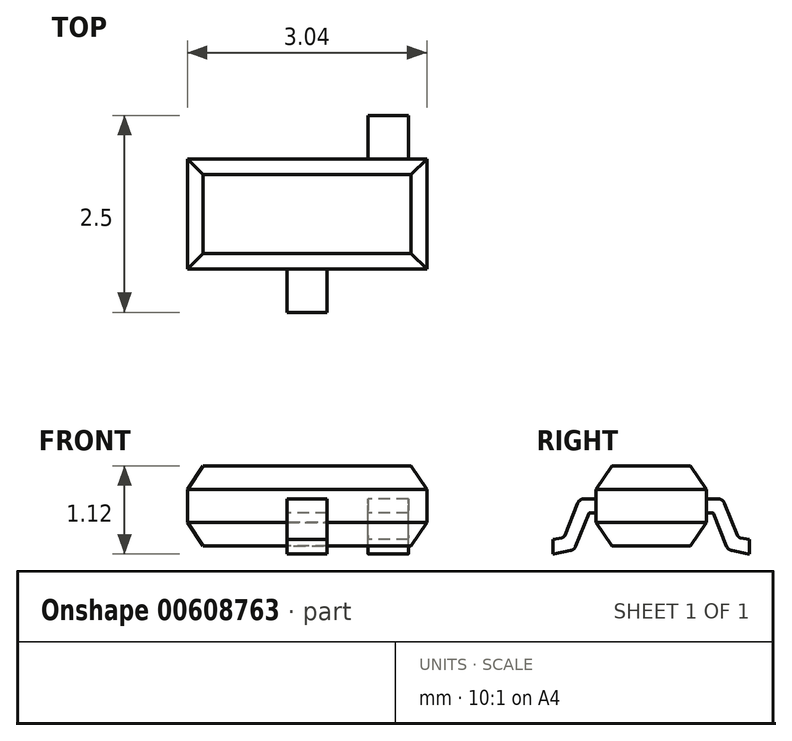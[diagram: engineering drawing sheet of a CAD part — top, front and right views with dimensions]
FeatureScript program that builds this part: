
annotation { "Feature Type Name" : "Feature", "Feature Type Description" : "" }
export const myFeature = defineFeature(function(context is Context, id is Id, definition is map)
    precondition{}
    {
        {
            var Q0;
            Q0=qCreatedBy(makeId("Top.planeOp"),FACE);
            cPlane(context, id + "F0", {"entities" : qUnion([Q0]), "cplaneType" : CPlaneType.OFFSET, "offset" : 0.1 * mm, "width" : 150 * mm, "height" : 150 * mm});
        }
        {
            var Q0;
            Q0=qCreatedBy(id+"F0.planeOp",FACE);
            var sketch = newSketch(context, id + "F1", { "sketchPlane" : qUnion([Q0])});
            skLineSegment(sketch, "E0.bottom", {"start": v(-1.52, 0.7) * mm, "end": v(1.52, 0.7) * mm});
            skLineSegment(sketch, "E0.top", {"start": v(-1.52, -0.7) * mm, "end": v(1.52, -0.7) * mm});
            skLineSegment(sketch, "E0.left", {"start": v(-1.52, 0.7) * mm, "end": v(-1.52, -0.7) * mm});
            skLineSegment(sketch, "E0.right", {"start": v(1.52, 0.7) * mm, "end": v(1.52, -0.7) * mm});
            skPoint(sketch, "E0.middle", {"position": v(0, 0) * mm});
            skSolve(sketch);
        }
        {
            var Q0;
            Q0=makeQuery(id+"F1.imprint","IMPRINT",FACE,{"disambiguationData":[TD([[makeQuery(id+"F1.imprint","IMPRINT",EDGE,{"derivedFrom":sQuery(id+"F1.wireOp",EDGE,"E0.bottom")}),-1.0]])]});
            extrude(context, id + "F2", {"entities" : qUnion([Q0]), "depth" : 1.02 * mm, "offsetDistance" : 25 * mm});
        }
        {
            var Q0;
            Q0=makeQuery(id+"F2.opExtrude","CAP_EDGE",EDGE,{"disambiguationData":[OSD([sQuery(id+"F1.wireOp",EDGE,"E0.left")])],"isStart":false});
            var Q1;
            Q1=makeQuery(id+"F2.opExtrude","CAP_EDGE",EDGE,{"disambiguationData":[OSD([sQuery(id+"F1.wireOp",EDGE,"E0.left")])],"isStart":true});
            var Q2;
            Q2=makeQuery(id+"F2.opExtrude","CAP_EDGE",EDGE,{"disambiguationData":[OSD([sQuery(id+"F1.wireOp",EDGE,"E0.right")])],"isStart":true});
            var Q3;
            Q3=makeQuery(id+"F2.opExtrude","CAP_EDGE",EDGE,{"disambiguationData":[OSD([sQuery(id+"F1.wireOp",EDGE,"E0.right")])],"isStart":false});
            chamfer(context, id + "F3", {"entities" : qUnion([Q0, Q1, Q2, Q3]), "chamferType" : ChamferType.TWO_OFFSETS, "width1" : 0.2 * mm, "oppositeDirection" : false, "width2" : 0.3 * mm, "tangentPropagation" : true});
        }
        {
            var Q0;
            Q0=makeQuery(id+"F2.opExtrude","CAP_EDGE",EDGE,{"disambiguationData":[OSD([sQuery(id+"F1.wireOp",EDGE,"E0.top")])],"isStart":false});
            var Q1;
            Q1=makeQuery(id+"F2.opExtrude","CAP_EDGE",EDGE,{"disambiguationData":[OSD([sQuery(id+"F1.wireOp",EDGE,"E0.top")])],"isStart":true});
            var Q2;
            Q2=makeQuery(id+"F2.opExtrude","CAP_EDGE",EDGE,{"disambiguationData":[OSD([sQuery(id+"F1.wireOp",EDGE,"E0.bottom")])],"isStart":true});
            var Q3;
            Q3=makeQuery(id+"F2.opExtrude","CAP_EDGE",EDGE,{"disambiguationData":[OSD([sQuery(id+"F1.wireOp",EDGE,"E0.bottom")])],"isStart":false});
            chamfer(context, id + "F4", {"entities" : qUnion([Q0, Q1, Q2, Q3]), "chamferType" : ChamferType.TWO_OFFSETS, "width1" : 0.2 * mm, "oppositeDirection" : false, "width2" : 0.3 * mm, "tangentPropagation" : true});
        }
        {
            var Q0;
            {var subQ0=sQuery(id+"F1.wireOp",EDGE,"E0.top");Q0=makeQuery(id+"F4.opChamfer","BLEND_EDGE",EDGE,{"blendedFrom":[makeQuery(id+"F2.opExtrude","CAP_EDGE",EDGE,{"disambiguationData":[OSD([subQ0])],"isStart":false}),makeQuery(id+"F2.opExtrude","CAP_FACE",FACE,{"disambiguationData":[OSD([sQuery(id+"F1.wireOp",EDGE,"E0.bottom"),subQ0,sQuery(id+"F1.wireOp",EDGE,"E0.left"),sQuery(id+"F1.wireOp",EDGE,"E0.right")])],"isStart":false})],"blendedInto":[makeQuery(id+"F2.opExtrude","CAP_FACE",FACE,{"disambiguationData":[OSD([sQuery(id+"F1.wireOp",EDGE,"E0.bottom"),subQ0,sQuery(id+"F1.wireOp",EDGE,"E0.left"),sQuery(id+"F1.wireOp",EDGE,"E0.right")])],"isStart":false})]});}
            cPoint(context, id + "F5", {"entities" : qUnion([Q0]), "parameter" : 0.5});
        }
        {
            var Q0;
            {var subQ0=sQuery(id+"F1.wireOp",EDGE,"E0.bottom");Q0=makeQuery(id+"F4.opChamfer","BLEND_EDGE",EDGE,{"blendedFrom":[makeQuery(id+"F2.opExtrude","CAP_EDGE",EDGE,{"disambiguationData":[OSD([subQ0])],"isStart":false}),makeQuery(id+"F2.opExtrude","CAP_FACE",FACE,{"disambiguationData":[OSD([subQ0,sQuery(id+"F1.wireOp",EDGE,"E0.top"),sQuery(id+"F1.wireOp",EDGE,"E0.left"),sQuery(id+"F1.wireOp",EDGE,"E0.right")])],"isStart":false})],"blendedInto":[makeQuery(id+"F2.opExtrude","CAP_FACE",FACE,{"disambiguationData":[OSD([subQ0,sQuery(id+"F1.wireOp",EDGE,"E0.top"),sQuery(id+"F1.wireOp",EDGE,"E0.left"),sQuery(id+"F1.wireOp",EDGE,"E0.right")])],"isStart":false})]});}
            cPoint(context, id + "F6", {"entities" : qUnion([Q0]), "parameter" : 0.5});
        }
        {
            var Q0;
            {var subQ0=sQuery(id+"F1.wireOp",EDGE,"E0.bottom");Q0=makeQuery(id+"F4.opChamfer","BLEND_EDGE",EDGE,{"blendedFrom":[makeQuery(id+"F2.opExtrude","CAP_EDGE",EDGE,{"disambiguationData":[OSD([subQ0])],"isStart":true}),makeQuery(id+"F2.opExtrude","CAP_FACE",FACE,{"disambiguationData":[OSD([subQ0,sQuery(id+"F1.wireOp",EDGE,"E0.top"),sQuery(id+"F1.wireOp",EDGE,"E0.left"),sQuery(id+"F1.wireOp",EDGE,"E0.right")])],"isStart":true})],"blendedInto":[makeQuery(id+"F2.opExtrude","CAP_FACE",FACE,{"disambiguationData":[OSD([subQ0,sQuery(id+"F1.wireOp",EDGE,"E0.top"),sQuery(id+"F1.wireOp",EDGE,"E0.left"),sQuery(id+"F1.wireOp",EDGE,"E0.right")])],"isStart":true})]});}
            cPoint(context, id + "F7", {"entities" : qUnion([Q0]), "parameter" : 0.5});
        }
        {
            var Q0;
            Q0 = qCreatedBy(id + "F5" ,VERTEX);
            var Q1;
            Q1 = qCreatedBy(id + "F6" ,VERTEX);
            var Q2;
            Q2 = qCreatedBy(id + "F7" ,VERTEX);
            cPlane(context, id + "F8", {"entities" : qUnion([Q0, Q1, Q2]), "cplaneType" : CPlaneType.THREE_POINT, "offset" : 25 * mm, "width" : 150 * mm, "height" : 150 * mm});
        }
        {
            var Q0;
            Q0=qCreatedBy(id+"F8.planeOp",FACE);
            var sketch = newSketch(context, id + "F9", { "sketchPlane" : qUnion([Q0])});
            skLineSegment(sketch, "E1", {"start": v(0, 0) * mm, "end": v(-2.5, 0) * mm, "construction": true});
            skLineSegment(sketch, "E2", {"start": v(-1.25, 0) * mm, "end": v(-1.25, 0.09) * mm});
            skLineSegment(sketch, "E3", {"start": v(-0.7, 0.61) * mm, "end": v(-0.85, 0.61) * mm, "construction": true});
            skLineSegment(sketch, "E4", {"start": v(-1.04, 0.13) * mm, "end": v(-0.85, 0.61) * mm, "construction": true});
            skArc(sketch, "E5.0.startCap", {"start": v(-0.96, 0.1) * mm, "mid": v(-0.98, 0.06) * mm, "end": v(-1.02, 0.04) * mm});
            skArc(sketch, "E5.0.endCap", {"start": v(-0.93, 0.64) * mm, "mid": v(-0.9, 0.68) * mm, "end": v(-0.85, 0.7) * mm});
            skLineSegment(sketch, "E5.0.left", {"start": v(-1.1, 0.24) * mm, "end": v(-0.93, 0.64) * mm});
            skLineSegment(sketch, "E5.0.right", {"start": v(-0.96, 0.1) * mm, "end": v(-0.8, 0.51) * mm});
            skArc(sketch, "E6.0.startCap", {"start": v(-1.23, 0) * mm, "mid": v(-1.24, 0) * mm, "end": v(-1.25, 0) * mm});
            skLineSegment(sketch, "E6.0.left", {"start": v(-1.25, 0.18) * mm, "end": v(-1.13, 0.2) * mm});
            skLineSegment(sketch, "E6.0.right", {"start": v(-1.23, 0) * mm, "end": v(-1.02, 0.04) * mm});
            skLineSegment(sketch, "E6.1.left", {"start": v(-0.7, 0.52) * mm, "end": v(-0.78, 0.52) * mm});
            skLineSegment(sketch, "E6.1.right", {"start": v(-0.7, 0.7) * mm, "end": v(-0.85, 0.7) * mm});
            skLineSegment(sketch, "E7", {"start": v(-0.7, 0.7) * mm, "end": v(-0.7, 0.52) * mm});
            skLineSegment(sketch, "E8", {"start": v(-1.25, 0.18) * mm, "end": v(-1.25, 0.18) * mm});
            skLineSegment(sketch, "E9.trimOffspring", {"start": v(-1.25, 0.09) * mm, "end": v(-1.25, 0) * mm});
            skLineSegment(sketch, "E10", {"start": v(-1.25, 0.09) * mm, "end": v(-1.25, 0.18) * mm});
            skPoint(sketch, "E11.visualSharp", {"position": v(-0.79, 0.52) * mm});
            skArc(sketch, "E11.filletArc", {"start": v(-0.78, 0.52) * mm, "mid": v(-0.79, 0.52) * mm, "end": v(-0.8, 0.51) * mm});
            skPoint(sketch, "E12.visualSharp", {"position": v(-1.1, 0.21) * mm});
            skArc(sketch, "E12.filletArc", {"start": v(-1.13, 0.2) * mm, "mid": v(-1.11, 0.22) * mm, "end": v(-1.1, 0.24) * mm});
            skSolve(sketch);
        }
        {
            var Q0;
            Q0=makeQuery(id+"F9.imprint","IMPRINT",FACE,{"disambiguationData":[TD([[makeQuery(id+"F9.imprint","IMPRINT",EDGE,{"derivedFrom":sQuery(id+"F9.wireOp",EDGE,"E5.0.left")}),-1.0]])]});
            extrude(context, id + "F10", {"entities" : qUnion([Q0]), "operationType" : NewBodyOperationType.ADD, "endBound" : BoundingType.SYMMETRIC, "depth" : 0.51 * mm, "offsetDistance" : 25 * mm});
        }
        {
            var Q0;
            Q0=qCreatedBy(id+"F8.planeOp",FACE);
            cPlane(context, id + "F11", {"entities" : qUnion([Q0]), "cplaneType" : CPlaneType.OFFSET, "offset" : 1.03 * mm, "width" : 150 * mm, "height" : 150 * mm});
        }
        {
            var Q0;
            Q0=qCreatedBy(id+"F11.planeOp",FACE);
            var sketch = newSketch(context, id + "F12", { "sketchPlane" : qUnion([Q0])});
            skArc(sketch, "E13.MirrorCS", {"start": v(1.23, 0) * mm, "mid": v(1.24, 0) * mm, "end": v(1.25, 0) * mm});
            skArc(sketch, "E14.MirrorCS", {"start": v(0.78, 0.52) * mm, "mid": v(0.79, 0.52) * mm, "end": v(0.8, 0.51) * mm});
            skArc(sketch, "E15.MirrorCS", {"start": v(0.93, 0.64) * mm, "mid": v(0.9, 0.68) * mm, "end": v(0.85, 0.7) * mm});
            skArc(sketch, "E16.MirrorCS", {"start": v(0.96, 0.1) * mm, "mid": v(0.98, 0.06) * mm, "end": v(1.02, 0.04) * mm});
            skArc(sketch, "E17.MirrorCS", {"start": v(1.13, 0.2) * mm, "mid": v(1.11, 0.22) * mm, "end": v(1.1, 0.24) * mm});
            skLineSegment(sketch, "E18.MirrorCS", {"start": v(1.25, 0.18) * mm, "end": v(1.13, 0.2) * mm});
            skLineSegment(sketch, "E19.MirrorCS", {"start": v(0.7, 0.52) * mm, "end": v(0.78, 0.52) * mm});
            skLineSegment(sketch, "E20.MirrorCS", {"start": v(1.25, 0) * mm, "end": v(1.25, 0.18) * mm});
            skLineSegment(sketch, "E21.MirrorCS", {"start": v(1.23, 0) * mm, "end": v(1.02, 0.04) * mm});
            skLineSegment(sketch, "E22.MirrorCS", {"start": v(0.96, 0.1) * mm, "end": v(0.8, 0.51) * mm});
            skLineSegment(sketch, "E23.MirrorCS", {"start": v(0.7, 0.7) * mm, "end": v(0.85, 0.7) * mm});
            skLineSegment(sketch, "E24.MirrorCS", {"start": v(1.1, 0.24) * mm, "end": v(0.93, 0.64) * mm});
            skLineSegment(sketch, "E25", {"start": v(0.7, 0.7) * mm, "end": v(0.7, 0.52) * mm});
            skSolve(sketch);
        }
        {
            var Q0;
            Q0 = qSketchRegion(id + "F12", true);
            extrude(context, id + "F13", {"entities" : qUnion([Q0]), "operationType" : NewBodyOperationType.ADD, "endBound" : BoundingType.SYMMETRIC, "depth" : 0.51 * mm, "offsetDistance" : 25 * mm});
        }
    });
